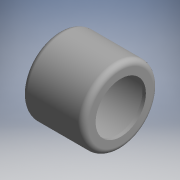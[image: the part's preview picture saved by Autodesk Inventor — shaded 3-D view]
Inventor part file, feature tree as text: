
AUTODESK INVENTOR PART (.ipt)
format: ipt  version: 2017.3 (Build 213256000, 256)  size: 146,944 bytes
history: native  units: mm (DEFAULTED — no unit token found)
features: other x21, revolve x1, sketch x1
ambient origin geometry x8: Origin, YZ Plane, XZ Plane, XY Plane, X Axis, Y Axis, Z Axis, Center Point
bodies: Solid1 (feature_tree)
feature tree (23):
  revolve  "Revolution1"  [1 undecoded]
  other  "IP_1_XY"
  other  "IP_1_YZ"
  other  "IP_1_ZX"
  other  "IP_1_X"
  other  "IP_1_Y"
  other  "IP_1_Z"
  other  "IP_1_Center"
  other  "IP_5_XY"
  other  "IP_5_YZ"
  other  "IP_5_ZX"
  other  "IP_5_X"
  other  "IP_5_Y"
  other  "IP_5_Z"
  other  "IP_5_Center"
  other  "IP_6_XY"
  other  "IP_6_YZ"
  other  "IP_6_ZX"
  other  "IP_6_X"
  other  "IP_6_Y"
  other  "IP_6_Z"
  other  "IP_6_Center"
  sketch  "Sketch_1"  dims[d0=360.0deg d1=0.0mm]
note: 1 required parameter value undecoded (feature->parameter linkage not recoverable at this tier; creation-order binding heuristic only, values carry confidence <= 0.55)
